# Revit family: LAMP_FIL 45 TW OPAL SURFACE
name_source: partatom
category: Luminarias
revit_build: Autodesk Revit 2018 (Build: 20170223_1515(x64)
units: mm (PartAtom-declared; Revit-internal decimal feet)

## family parameters
Anfitrión = Cara
Compartido = No
Corte con vacíos al cargar = No
Cota de conector redondo = Diámetro de uso
Origen de luz = Sí
Punto de cálculo de habitación = No
Tipo de pieza = Normal

## types (9) — shared parameters
CRI = 80
Cambio de temperatura de color de luz atenuada = <Ninguno>
Elevación por defecto = 1219 mm
Fabricante = LAMP
Filtro de color = 16777215
Gear = Electronic
IEE = A+
Initial color = 2700-6500K
Installation instructions = https://www.lamp.es
Insulation class = I
LED Lifetime = 50.000 L80 B10
Lamp = MID-POWER LED
Last update = 31/03/2021
MacAdam = 3
Manufacturer URL = http://www.lamp.es
Manufacturer country = Spain
Manufacturer name = LAMP
Material difusor = LAMP_PC Difusor Opal Fil
Material suspension = LAMP_Acero genérico
Power Supply = 220-240V 50/60Hz
Product URL = https://www.lamp.es
Product datasheet = http://www.lamp.es
Protection rating = IP20 / IK07
Type = MID POWER OSRAM
Ángulo de inclinación = -90.00°

## per-type parameters (varying)
| type | Archivo de red fotométrica | Descripción | Dimensions | Efficacy | Finish | Longitud | Longitud de línea de emisión | Material perfil | Modelo | Plum | Power | Product code | Weight |
| 2800LM 2700-6500K DALI BLACK | F41SF112MOOP8TWDB_4000k.IES | FIL45 SUR 1120 2800 TW OPAL DALI BK. | 1120x45x80 | 96 lm/W | Matte black RAL 9011 | 1120 mm  [stored 3.67454 ft] | 1120 mm  [stored 3.67454 ft] | LAMP_Aluminio Perfil Fil NG | F41SF112MOOP8TWDB | 31 W | 27 W | F41SF112MOOP8TWDB | 2.61 kg |
| 2800LM 2700-6500K DALI GREY | F41SF112MOOP8TWDG_4000k.IES | FIL45 SUR 1120 2800 TW OPAL DALI GR. | 1120x45x80 | 96 lm/W | Gloss grey | 1120 mm  [stored 3.67454 ft] | 1120 mm  [stored 3.67454 ft] | LAMP_Aluminio Perfil Fil GR | F41SF112MOOP8TWDG | 31 W | 27 W | F41SF112MOOP8TWDG | 2.61 kg |
| 2800LM 2700-6500K DALI WHITE | F41SF112MOOP8TWDW_4000k.IES | FIL45 SUR 1120 2800 TW OPAL DALI WH. | 1120x45x80 | 96 lm/W | Matte white RAL 9010 | 1120 mm  [stored 3.67454 ft] | 1120 mm  [stored 3.67454 ft] | LAMP_Aluminio Perfil Fil BL | F41SF112MOOP8TWDW | 31 W | 27 W | F41SF112MOOP8TWDW | 2.61 kg |
| 4200LM 2700-6500K DALI BLACK | F41SF168MOOP8TWDB_4000k.IES | FIL45 SUR 1680 4200 TW OPAL DALI BK. | 1680x45x80 | 93 lm/W | Matte black RAL 9011 | 1680 mm  [stored 5.51181 ft] | 1680 mm  [stored 5.51181 ft] | LAMP_Aluminio Perfil Fil NG | F41SF168MOOP8TWDB | 47 W | 41 W | F41SF168MOOP8TWDB | 3.77 kg |
| 4200LM 2700-6500K DALI GREY | F41SF168MOOP8TWDG_4000k.IES | FIL45 SUR 1680 4200 TW OPAL DALI GR. | 1680x45x80 | 93 lm/W | Gloss grey | 1680 mm  [stored 5.51181 ft] | 1680 mm  [stored 5.51181 ft] | LAMP_Aluminio Perfil Fil GR | F41SF168MOOP8TWDG | 47 W | 41 W | F41SF168MOOP8TWDG | 3.77 kg |
| 4200LM 2700-6500K DALI WHITE | F41SF168MOOP8TWDW_4000k.IES | FIL45 SUR 1680 4200 TW OPAL DALI WH. | 1680x45x80 | 93 lm/W | Matte white RAL 9010 | 1680 mm  [stored 5.51181 ft] | 1680 mm  [stored 5.51181 ft] | LAMP_Aluminio Perfil Fil BL | F41SF168MOOP8TWDW | 47 W | 41 W | F41SF168MOOP8TWDW | 3.77 kg |
| 5600LM 2700-6500K DALI BLACK | F41SF224MOOP8TWDB_4000k.IES | FIL45 SUR 2240 5600 TW OPAL DALI BK. | 2240x45x80 | 96 lm/W | Matte black RAL 9011 | 2240 mm  [stored 7.34908 ft] | 2240 mm  [stored 7.34908 ft] | LAMP_Aluminio Perfil Fil NG | F41SF224MOOP8TWDB | 61 W | 55 W | F41SF224MOOP8TWDB | 5.21 kg |
| 5600LM 2700-6500K DALI GREY | F41SF224MOOP8TWDG_4000k.IES | FIL45 SUR 2240 5600 TW OPAL DALI GR. | 2240x45x80 | 96 lm/W | Gloss grey | 2240 mm  [stored 7.34908 ft] | 2240 mm  [stored 7.34908 ft] | LAMP_Aluminio Perfil Fil GR | F41SF224MOOP8TWDG | 61 W | 55 W | F41SF224MOOP8TWDG | 5.21 kg |
| 5600LM 2700-6500K DALI WHITE | F41SF224MOOP8TWDW_4000k.IES | FIL45 SUR 2240 5600 TW OPAL DALI WH. | 2240x45x80 | 96 lm/W | Matte white RAL 9010 | 2240 mm  [stored 7.34908 ft] | 2240 mm  [stored 7.34908 ft] | LAMP_Aluminio Perfil Fil BL | F41SF224MOOP8TWDW | 61 W | 55 W | F41SF224MOOP8TWDW | 5.21 kg |

note: [stored X ft] marks values corroborated as IEEE doubles in the binary element streams (Revit-internal decimal feet)
